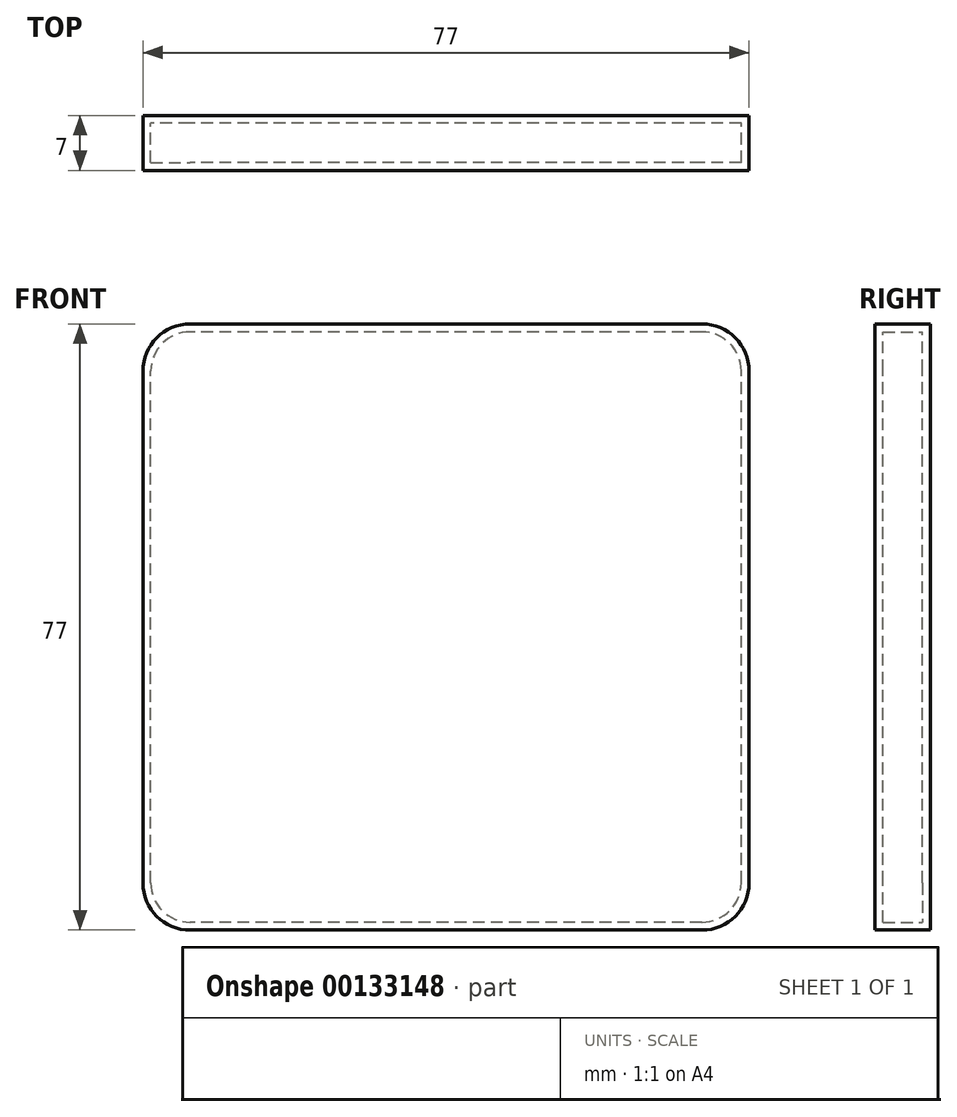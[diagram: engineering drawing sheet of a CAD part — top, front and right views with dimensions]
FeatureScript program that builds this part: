
annotation { "Feature Type Name" : "Feature", "Feature Type Description" : "" }
export const myFeature = defineFeature(function(context is Context, id is Id, definition is map)
    precondition{}
    {
        {
            var Q0;
            Q0=qCreatedBy(makeId("Front.planeOp"),FACE);
            var sketch = newSketch(context, id + "F0", { "sketchPlane" : qUnion([Q0])});
            skLineSegment(sketch, "E0.bottom", {"start": v(32.5, -37.5) * mm, "end": v(-32.5, -37.5) * mm});
            skLineSegment(sketch, "E0.top", {"start": v(32.5, 37.5) * mm, "end": v(-32.5, 37.5) * mm});
            skLineSegment(sketch, "E0.left", {"start": v(37.5, -32.5) * mm, "end": v(37.5, 32.5) * mm});
            skLineSegment(sketch, "E0.right", {"start": v(-37.5, -32.5) * mm, "end": v(-37.5, 32.5) * mm});
            skPoint(sketch, "E0.middle", {"position": v(0, 0) * mm});
            skLineSegment(sketch, "E1.bottom", {"start": v(32.5, -38.5) * mm, "end": v(-32.5, -38.5) * mm});
            skLineSegment(sketch, "E1.top", {"start": v(32.5, 38.5) * mm, "end": v(-32.5, 38.5) * mm});
            skLineSegment(sketch, "E1.left", {"start": v(38.5, -32.5) * mm, "end": v(38.5, 32.5) * mm});
            skLineSegment(sketch, "E1.right", {"start": v(-38.5, -32.5) * mm, "end": v(-38.5, 32.5) * mm});
            skArc(sketch, "E2", {"start": v(-32.5, 37.5) * mm, "mid": v(-36.04, 36.04) * mm, "end": v(-37.5, 32.5) * mm});
            skArc(sketch, "E3", {"start": v(-32.5, 38.5) * mm, "mid": v(-36.74, 36.74) * mm, "end": v(-38.5, 32.5) * mm});
            skArc(sketch, "E4", {"start": v(37.5, 32.5) * mm, "mid": v(36.04, 36.04) * mm, "end": v(32.5, 37.5) * mm});
            skArc(sketch, "E5", {"start": v(38.5, 32.5) * mm, "mid": v(36.74, 36.74) * mm, "end": v(32.5, 38.5) * mm});
            skArc(sketch, "E6", {"start": v(32.5, -37.5) * mm, "mid": v(36.04, -36.04) * mm, "end": v(37.5, -32.5) * mm});
            skArc(sketch, "E7", {"start": v(32.5, -38.5) * mm, "mid": v(36.74, -36.74) * mm, "end": v(38.5, -32.5) * mm});
            skArc(sketch, "E8", {"start": v(-37.5, -32.5) * mm, "mid": v(-36.04, -36.04) * mm, "end": v(-32.5, -37.5) * mm});
            skArc(sketch, "E9", {"start": v(-38.5, -32.5) * mm, "mid": v(-36.74, -36.74) * mm, "end": v(-32.5, -38.5) * mm});
            skSolve(sketch);
        }
        {
            var Q0;
            Q0=makeQuery(id+"F0.imprint","IMPRINT",FACE,{"disambiguationData":[TD([[makeQuery(id+"F0.imprint","IMPRINT",EDGE,{"derivedFrom":sQuery(id+"F0.wireOp",EDGE,"E0.bottom")}),1.0]])]});
            extrude(context, id + "F1", {"entities" : qUnion([Q0]), "depth" : 5 * mm});
        }
        {
            var Q0;
            Q0=makeQuery(id+"F1.opExtrude","CAP_FACE",FACE,{"disambiguationData":[OSD([sQuery(id+"F0.wireOp",EDGE,"E0.bottom"),sQuery(id+"F0.wireOp",EDGE,"E0.top"),sQuery(id+"F0.wireOp",EDGE,"E0.left"),sQuery(id+"F0.wireOp",EDGE,"E0.right"),sQuery(id+"F0.wireOp",EDGE,"E1.bottom"),sQuery(id+"F0.wireOp",EDGE,"E1.top"),sQuery(id+"F0.wireOp",EDGE,"E1.left"),sQuery(id+"F0.wireOp",EDGE,"E1.right"),sQuery(id+"F0.wireOp",EDGE,"E2"),sQuery(id+"F0.wireOp",EDGE,"E3"),sQuery(id+"F0.wireOp",EDGE,"E4"),sQuery(id+"F0.wireOp",EDGE,"E5"),sQuery(id+"F0.wireOp",EDGE,"E6"),sQuery(id+"F0.wireOp",EDGE,"E7"),sQuery(id+"F0.wireOp",EDGE,"E8"),sQuery(id+"F0.wireOp",EDGE,"E9")])],"isStart":false});
            var sketch = newSketch(context, id + "F2", { "sketchPlane" : qUnion([Q0])});
            skSolve(sketch);
        }
        {
            var Q0;
            Q0=makeQuery(id+"F2.imprint","IMPRINT",FACE,{"disambiguationData":[TD([[makeQuery(id+"F2.imprint","IMPRINT",EDGE,{"derivedFrom":makeQuery(id+"F1.opExtrude","CAP_EDGE",EDGE,{"disambiguationData":[OSD([sQuery(id+"F0.wireOp",EDGE,"E0.bottom")])],"isStart":false})}),1.0]])]});
            var Q1;
            Q1=qSketchRegion(id+"F2",true);
            var Q2;
            Q2=makeQuery(id+"F2.imprint","IMPRINT",FACE,{"disambiguationData":[TD([[makeQuery(id+"F2.imprint","IMPRINT",EDGE,{"derivedFrom":makeQuery(id+"F1.opExtrude","CAP_EDGE",EDGE,{"disambiguationData":[OSD([sQuery(id+"F0.wireOp",EDGE,"E0.bottom")])],"isStart":false})}),-1.0]])]});
            extrude(context, id + "F3", {"entities" : qUnion([Q0, Q1, Q2]), "operationType" : NewBodyOperationType.ADD, "depth" : 1 * mm});
        }
        {
            var Q0;
            Q0=makeQuery(id+"F1.opExtrude","CAP_FACE",FACE,{"disambiguationData":[OSD([sQuery(id+"F0.wireOp",EDGE,"E0.bottom"),sQuery(id+"F0.wireOp",EDGE,"E0.top"),sQuery(id+"F0.wireOp",EDGE,"E0.left"),sQuery(id+"F0.wireOp",EDGE,"E0.right"),sQuery(id+"F0.wireOp",EDGE,"E1.bottom"),sQuery(id+"F0.wireOp",EDGE,"E1.top"),sQuery(id+"F0.wireOp",EDGE,"E1.left"),sQuery(id+"F0.wireOp",EDGE,"E1.right"),sQuery(id+"F0.wireOp",EDGE,"E2"),sQuery(id+"F0.wireOp",EDGE,"E3"),sQuery(id+"F0.wireOp",EDGE,"E4"),sQuery(id+"F0.wireOp",EDGE,"E5"),sQuery(id+"F0.wireOp",EDGE,"E6"),sQuery(id+"F0.wireOp",EDGE,"E7"),sQuery(id+"F0.wireOp",EDGE,"E8"),sQuery(id+"F0.wireOp",EDGE,"E9")])],"isStart":true});
            var sketch = newSketch(context, id + "F4", { "sketchPlane" : qUnion([Q0])});
            skSolve(sketch);
        }
        {
            var Q0;
            Q0=makeQuery(id+"F4.imprint","IMPRINT",FACE,{"disambiguationData":[TD([[makeQuery(id+"F4.imprint","IMPRINT",EDGE,{"derivedFrom":makeQuery(id+"F1.opExtrude","CAP_EDGE",EDGE,{"disambiguationData":[OSD([sQuery(id+"F0.wireOp",EDGE,"E0.bottom")])],"isStart":true})}),-1.0]])]});
            var Q1;
            Q1=makeQuery(id+"F4.imprint","IMPRINT",FACE,{"disambiguationData":[TD([[makeQuery(id+"F4.imprint","IMPRINT",EDGE,{"derivedFrom":makeQuery(id+"F1.opExtrude","CAP_EDGE",EDGE,{"disambiguationData":[OSD([sQuery(id+"F0.wireOp",EDGE,"E0.bottom")])],"isStart":true})}),1.0]])]});
            extrude(context, id + "F5", {"entities" : qUnion([Q0, Q1]), "operationType" : NewBodyOperationType.ADD, "depth" : 1 * mm});
        }
    });
